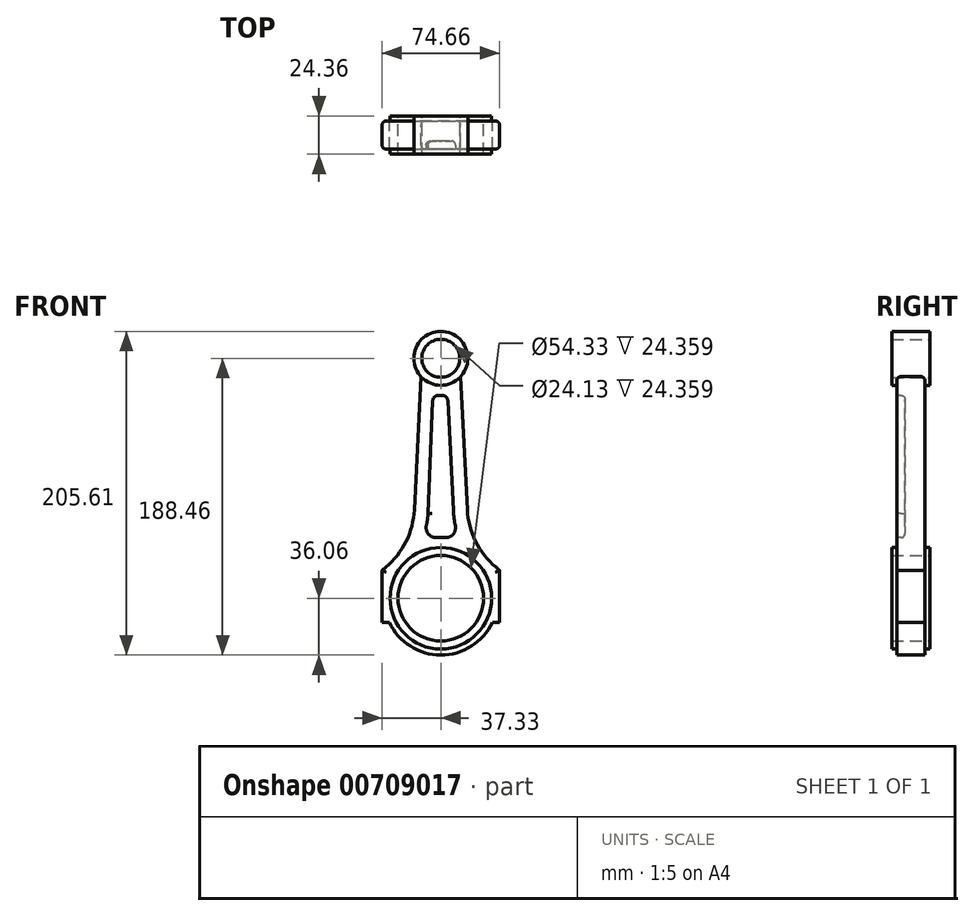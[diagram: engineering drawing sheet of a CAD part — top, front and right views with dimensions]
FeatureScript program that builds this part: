
annotation { "Feature Type Name" : "Feature", "Feature Type Description" : "" }
export const myFeature = defineFeature(function(context is Context, id is Id, definition is map)
    precondition{}
    {
        {
            var Q0;
            Q0=qCreatedBy(makeId("Front.planeOp"),FACE);
            var sketch = newSketch(context, id + "F0", { "sketchPlane" : qUnion([Q0])});
            skLineSegment(sketch, "E0", {"start": v(0, 0) * mm, "end": v(0, 152.4) * mm, "construction": true});
            skCircle(sketch, "E1", {"center": v(0, 0) * mm, "radius": 27.17 * mm});
            skCircle(sketch, "E2", {"center": v(0, 152.4) * mm, "radius": 12.06 * mm});
            skCircle(sketch, "E3", {"center": v(0, 0) * mm, "radius": 32.25 * mm});
            skArc(sketch, "E4", {"start": v(-32.68, -15.24) * mm, "mid": v(0, -36.06) * mm, "end": v(32.68, -15.24) * mm});
            skCircle(sketch, "E5.0", {"center": v(0, 152.4) * mm, "radius": 17.14 * mm});
            skLineSegment(sketch, "E6", {"start": v(0, 0) * mm, "end": v(-37.33, 0) * mm});
            skLineSegment(sketch, "E7", {"start": v(-37.33, 0) * mm, "end": v(-37.33, 17.78) * mm});
            skLineSegment(sketch, "E8", {"start": v(-17.9, 34.01) * mm, "end": v(-37.33, 17.78) * mm});
            skLineSegment(sketch, "E9", {"start": v(-17.9, 34.01) * mm, "end": v(-12.64, 140.81) * mm});
            skLineSegment(sketch, "E10.MirrorCS", {"start": v(17.9, 34.01) * mm, "end": v(12.64, 140.81) * mm});
            skLineSegment(sketch, "E11.MirrorCS", {"start": v(17.9, 34.01) * mm, "end": v(37.33, 17.78) * mm});
            skLineSegment(sketch, "E12.MirrorCS", {"start": v(37.33, 0) * mm, "end": v(37.33, 17.78) * mm});
            skLineSegment(sketch, "E13.MirrorCS", {"start": v(0, 0) * mm, "end": v(37.33, 0) * mm});
            skLineSegment(sketch, "E14", {"start": v(-37.33, 0) * mm, "end": v(-37.33, -15.24) * mm});
            skLineSegment(sketch, "E15", {"start": v(-37.33, -15.24) * mm, "end": v(-32.68, -15.24) * mm});
            skLineSegment(sketch, "E16.MirrorCS", {"start": v(37.33, -15.24) * mm, "end": v(32.68, -15.24) * mm});
            skLineSegment(sketch, "E17.MirrorCS", {"start": v(37.33, 0) * mm, "end": v(37.33, -15.24) * mm});
            skPoint(sketch, "E18.orphan", {"position": v(-12.07, 152.4) * mm});
            skPoint(sketch, "E19.orphan", {"position": v(12.07, 152.4) * mm});
            skSolve(sketch);
        }
        {
            var Q0;
            {var subQ0=sQuery(id+"F0.wireOp",EDGE,"E6");var subQ1=sQuery(id+"F0.wireOp",EDGE,"E1");var subQ2=makeQuery(id+"F0.imprint","INTERSECT",VERTEX,{"derivedFrom":[subQ1,subQ0]});Q0=makeQuery(id+"F0.imprint","IMPRINT",FACE,{"disambiguationData":[TD([[makeQuery(id+"F0.imprint","IMPRINT",EDGE,{"disambiguationData":[TD([[subQ2,1.0]])],"derivedFrom":subQ1}),-1.0]])]});}
            extrude(context, id + "F1", {"entities" : qUnion([Q0]), "endBound" : BoundingType.SYMMETRIC, "depth" : 24.36 * mm, "offsetDistance" : 25.4 * mm});
        }
        {
            var Q0;
            {var subQ0=sQuery(id+"F0.wireOp",EDGE,"E6");var subQ1=sQuery(id+"F0.wireOp",EDGE,"E1");var subQ2=makeQuery(id+"F0.imprint","INTERSECT",VERTEX,{"derivedFrom":[subQ1,subQ0]});Q0=makeQuery(id+"F0.imprint","IMPRINT",FACE,{"disambiguationData":[TD([[makeQuery(id+"F0.imprint","IMPRINT",EDGE,{"disambiguationData":[TD([[subQ2,-1.0]])],"derivedFrom":subQ1}),-1.0]])]});}
            extrude(context, id + "F2", {"entities" : qUnion([Q0]), "endBound" : BoundingType.SYMMETRIC, "depth" : 24.36 * mm, "offsetDistance" : 25.4 * mm});
        }
        {
            var Q0;
            {var subQ0=sQuery(id+"F0.wireOp",EDGE,"E7");Q0=makeQuery(id+"F0.imprint","IMPRINT",FACE,{"disambiguationData":[TD([[makeQuery(id+"F0.imprint","IMPRINT",EDGE,{"derivedFrom":subQ0}),-1.0]])]});}
            extrude(context, id + "F3", {"entities" : qUnion([Q0]), "operationType" : NewBodyOperationType.ADD, "endBound" : BoundingType.SYMMETRIC, "depth" : 17.78 * mm, "offsetDistance" : 25.4 * mm});
        }
        {
            var Q0;
            Q0=makeQuery(id+"F0.imprint","IMPRINT",FACE,{"disambiguationData":[TD([[makeQuery(id+"F0.imprint","IMPRINT",EDGE,{"derivedFrom":sQuery(id+"F0.wireOp",EDGE,"E2")}),-1.0]])]});
            extrude(context, id + "F4", {"entities" : qUnion([Q0]), "operationType" : NewBodyOperationType.ADD, "endBound" : BoundingType.SYMMETRIC, "depth" : 24.36 * mm, "offsetDistance" : 25.4 * mm});
        }
        {
            var Q0;
            Q0=makeQuery(id+"F0.imprint","IMPRINT",FACE,{"disambiguationData":[TD([[makeQuery(id+"F0.imprint","IMPRINT",EDGE,{"derivedFrom":sQuery(id+"F0.wireOp",EDGE,"E4")}),1.0]])]});
            extrude(context, id + "F5", {"entities" : qUnion([Q0]), "operationType" : NewBodyOperationType.ADD, "endBound" : BoundingType.SYMMETRIC, "depth" : 17.78 * mm, "offsetDistance" : 25.4 * mm});
        }
        {
            var Q0;
            Q0=makeQuery(id+"F3.opExtrude","SWEPT_EDGE",EDGE,{"disambiguationData":[OSD([sQuery(id+"F0.wireOp",EDGE,"E10.MirrorCS"),sQuery(id+"F0.wireOp",EDGE,"E11.MirrorCS")])]});
            var Q1;
            Q1=makeQuery(id+"F3.opExtrude","SWEPT_EDGE",EDGE,{"disambiguationData":[OSD([sQuery(id+"F0.wireOp",EDGE,"E8"),sQuery(id+"F0.wireOp",EDGE,"E9")])]});
            fillet(context, id + "F6", {"entities" : qUnion([Q0, Q1]), "radius" : 50.8 * mm, "tangentPropagation" : true, "allowEdgeOverflow" : false});
        }
        {
            var Q0;
            Q0=makeQuery(id+"F3.opExtrude","CAP_EDGE",EDGE,{"disambiguationData":[OSD([sQuery(id+"F0.wireOp",EDGE,"E10.MirrorCS")])],"isStart":true});
            var Q1;
            Q1=makeQuery(id+"F3.opExtrude","CAP_EDGE",EDGE,{"disambiguationData":[OSD([sQuery(id+"F0.wireOp",EDGE,"E9")])],"isStart":true});
            var Q2;
            Q2=makeQuery(id+"F3.opExtrude","CAP_EDGE",EDGE,{"disambiguationData":[OSD([sQuery(id+"F0.wireOp",EDGE,"E9")])],"isStart":false});
            var Q3;
            {var subQ0=sQuery(id+"F0.wireOp",EDGE,"E11.MirrorCS");var subQ1=sQuery(id+"F0.wireOp",EDGE,"E10.MirrorCS");Q3=makeQuery(id+"F6.opFillet","BLEND_EDGE",EDGE,{"blendedFrom":[makeQuery(id+"F3.opExtrude","SWEPT_EDGE",EDGE,{"disambiguationData":[OSD([subQ1,subQ0])]}),makeQuery(id+"F3.opExtrude","CAP_FACE",FACE,{"disambiguationData":[OSD([sQuery(id+"F0.wireOp",EDGE,"E3"),sQuery(id+"F0.wireOp",EDGE,"E5.0"),sQuery(id+"F0.wireOp",EDGE,"E6"),sQuery(id+"F0.wireOp",EDGE,"E7"),sQuery(id+"F0.wireOp",EDGE,"E8"),sQuery(id+"F0.wireOp",EDGE,"E9"),subQ1,subQ0,sQuery(id+"F0.wireOp",EDGE,"E12.MirrorCS"),sQuery(id+"F0.wireOp",EDGE,"E13.MirrorCS")])],"isStart":false})],"blendedInto":[makeQuery(id+"F3.opExtrude","CAP_FACE",FACE,{"disambiguationData":[OSD([sQuery(id+"F0.wireOp",EDGE,"E3"),sQuery(id+"F0.wireOp",EDGE,"E5.0"),sQuery(id+"F0.wireOp",EDGE,"E6"),sQuery(id+"F0.wireOp",EDGE,"E7"),sQuery(id+"F0.wireOp",EDGE,"E8"),sQuery(id+"F0.wireOp",EDGE,"E9"),subQ1,subQ0,sQuery(id+"F0.wireOp",EDGE,"E12.MirrorCS"),sQuery(id+"F0.wireOp",EDGE,"E13.MirrorCS")])],"isStart":false})]});}
            var Q4;
            Q4=makeQuery(id+"F3.opExtrude","CAP_EDGE",EDGE,{"disambiguationData":[OSD([sQuery(id+"F0.wireOp",EDGE,"E12.MirrorCS")])],"isStart":false});
            var Q5;
            Q5=makeQuery(id+"F5.opExtrude","CAP_EDGE",EDGE,{"disambiguationData":[OSD([sQuery(id+"F0.wireOp",EDGE,"E17.MirrorCS")])],"isStart":false});
            var Q6;
            Q6=makeQuery(id+"F3.opExtrude","CAP_EDGE",EDGE,{"disambiguationData":[OSD([sQuery(id+"F0.wireOp",EDGE,"E12.MirrorCS")])],"isStart":true});
            var Q7;
            Q7=makeQuery(id+"F5.opExtrude","CAP_EDGE",EDGE,{"disambiguationData":[OSD([sQuery(id+"F0.wireOp",EDGE,"E17.MirrorCS")])],"isStart":true});
            var Q8;
            Q8=makeQuery(id+"F3.opExtrude","CAP_EDGE",EDGE,{"disambiguationData":[OSD([sQuery(id+"F0.wireOp",EDGE,"E7")])],"isStart":false});
            var Q9;
            Q9=makeQuery(id+"F3.opExtrude","CAP_EDGE",EDGE,{"disambiguationData":[OSD([sQuery(id+"F0.wireOp",EDGE,"E7")])],"isStart":true});
            var Q10;
            Q10=makeQuery(id+"F5.opExtrude","CAP_EDGE",EDGE,{"disambiguationData":[OSD([sQuery(id+"F0.wireOp",EDGE,"E14")])],"isStart":true});
            var Q11;
            Q11=makeQuery(id+"F5.opExtrude","CAP_EDGE",EDGE,{"disambiguationData":[OSD([sQuery(id+"F0.wireOp",EDGE,"E14")])],"isStart":false});
            fillet(context, id + "F7", {"entities" : qUnion([Q0, Q1, Q2, Q3, Q4, Q5, Q6, Q7, Q8, Q9, Q10, Q11]), "radius" : 2.54 * mm, "tangentPropagation" : true, "allowEdgeOverflow" : false});
        }
        {
            var Q0;
            Q0=makeQuery(id+"F3.opExtrude","CAP_FACE",FACE,{"disambiguationData":[OSD([sQuery(id+"F0.wireOp",EDGE,"E3"),sQuery(id+"F0.wireOp",EDGE,"E5.0"),sQuery(id+"F0.wireOp",EDGE,"E6"),sQuery(id+"F0.wireOp",EDGE,"E7"),sQuery(id+"F0.wireOp",EDGE,"E8"),sQuery(id+"F0.wireOp",EDGE,"E9"),sQuery(id+"F0.wireOp",EDGE,"E10.MirrorCS"),sQuery(id+"F0.wireOp",EDGE,"E11.MirrorCS"),sQuery(id+"F0.wireOp",EDGE,"E12.MirrorCS"),sQuery(id+"F0.wireOp",EDGE,"E13.MirrorCS")])],"isStart":false});
            var sketch = newSketch(context, id + "F8", { "sketchPlane" : qUnion([Q0])});
            skLineSegment(sketch, "E20.0", {"start": v(7.93, 55.78) * mm, "end": v(4.5, 125.3) * mm});
            skArc(sketch, "E20.1", {"start": v(9.2, 46.18) * mm, "mid": v(8.37, 50.96) * mm, "end": v(7.93, 55.78) * mm});
            skArc(sketch, "E20.3", {"start": v(-8.05, 53.92) * mm, "mid": v(-8.5, 50.03) * mm, "end": v(-9.2, 46.18) * mm});
            skArc(sketch, "E20.4", {"start": v(-2.56, 38.51) * mm, "mid": v(0, 38.6) * mm, "end": v(2.56, 38.51) * mm});
            skArc(sketch, "E21.0", {"start": v(-1.17, 128.93) * mm, "mid": v(-0.29, 128.9) * mm, "end": v(0.6, 128.91) * mm});
            skLineSegment(sketch, "E22.trimOffspring", {"start": v(-5.17, 125.28) * mm, "end": v(-8.05, 53.92) * mm});
            skPoint(sketch, "E23.visualSharp", {"position": v(-12.1, 36.65) * mm});
            skArc(sketch, "E23.filletArc", {"start": v(-9.2, 46.18) * mm, "mid": v(-7.79, 40.7) * mm, "end": v(-2.56, 38.51) * mm});
            skPoint(sketch, "E24.visualSharp", {"position": v(12.1, 36.65) * mm});
            skArc(sketch, "E24.filletArc", {"start": v(2.56, 38.51) * mm, "mid": v(7.79, 40.7) * mm, "end": v(9.2, 46.18) * mm});
            skPoint(sketch, "E25.visualSharp", {"position": v(-5, 129.44) * mm});
            skArc(sketch, "E25.filletArc", {"start": v(-1.17, 128.93) * mm, "mid": v(-3.93, 127.94) * mm, "end": v(-5.17, 125.28) * mm});
            skPoint(sketch, "E26.visualSharp", {"position": v(4.3, 129.3) * mm});
            skArc(sketch, "E26.filletArc", {"start": v(4.5, 125.3) * mm, "mid": v(3.29, 127.9) * mm, "end": v(0.6, 128.91) * mm});
            skSolve(sketch);
        }
        {
            var Q0;
            Q0=makeQuery(id+"F8.imprint","IMPRINT",FACE,{"disambiguationData":[TD([[makeQuery(id+"F8.imprint","IMPRINT",EDGE,{"derivedFrom":sQuery(id+"F8.wireOp",EDGE,"E20.0")}),1.0]])]});
            extrude(context, id + "F9", {"entities" : qUnion([Q0]), "operationType" : NewBodyOperationType.REMOVE, "oppositeDirection" : true, "depth" : 5.08 * mm, "offsetDistance" : 25.4 * mm});
        }
        {
            var Q0;
            Q0=makeQuery(id+"FBvjnZQbK2bqoB8_2.1.F9.boolean.opBoolean","COPY",FACE,{"derivedFrom":makeQuery(id+"FBvjnZQbK2bqoB8_2.1.F9.opExtrude","CAP_FACE",FACE,{"disambiguationData":[OSD([sQuery(id+"F8.wireOp",EDGE,"E20.0"),sQuery(id+"F8.wireOp",EDGE,"E20.1"),sQuery(id+"F8.wireOp",EDGE,"E20.3"),sQuery(id+"F8.wireOp",EDGE,"E20.4"),sQuery(id+"F8.wireOp",EDGE,"E21.0"),sQuery(id+"F8.wireOp",EDGE,"E22.trimOffspring"),sQuery(id+"F8.wireOp",EDGE,"E23.filletArc"),sQuery(id+"F8.wireOp",EDGE,"E24.filletArc"),sQuery(id+"F8.wireOp",EDGE,"E25.filletArc"),sQuery(id+"F8.wireOp",EDGE,"E26.filletArc")])],"isStart":false})});
            var Q1;
            Q1=makeQuery(id+"FBvjnZQbK2bqoB8_2.1.F9.boolean.opBoolean","COPY",EDGE,{"derivedFrom":makeQuery(id+"FBvjnZQbK2bqoB8_2.1.F9.opExtrude","CAP_EDGE",EDGE,{"disambiguationData":[OSD([sQuery(id+"F8.wireOp",EDGE,"E22.trimOffspring")])],"isStart":true})});
            var Q2;
            Q2=makeQuery(id+"F9.boolean.opBoolean","COPY",FACE,{"derivedFrom":makeQuery(id+"F9.opExtrude","CAP_FACE",FACE,{"disambiguationData":[OSD([sQuery(id+"F8.wireOp",EDGE,"E20.0"),sQuery(id+"F8.wireOp",EDGE,"E20.1"),sQuery(id+"F8.wireOp",EDGE,"E20.3"),sQuery(id+"F8.wireOp",EDGE,"E20.4"),sQuery(id+"F8.wireOp",EDGE,"E21.0"),sQuery(id+"F8.wireOp",EDGE,"E22.trimOffspring"),sQuery(id+"F8.wireOp",EDGE,"E23.filletArc"),sQuery(id+"F8.wireOp",EDGE,"E24.filletArc"),sQuery(id+"F8.wireOp",EDGE,"E25.filletArc"),sQuery(id+"F8.wireOp",EDGE,"E26.filletArc")])],"isStart":false})});
            var Q3;
            Q3=makeQuery(id+"F9.boolean.opBoolean","COPY",EDGE,{"derivedFrom":makeQuery(id+"F9.opExtrude","CAP_EDGE",EDGE,{"disambiguationData":[OSD([sQuery(id+"F8.wireOp",EDGE,"E25.filletArc")])],"isStart":true})});
            fillet(context, id + "F10", {"entities" : qUnion([Q0, Q1, Q2, Q3]), "radius" : 2.54 * mm, "tangentPropagation" : true, "allowEdgeOverflow" : false});
        }
    });
